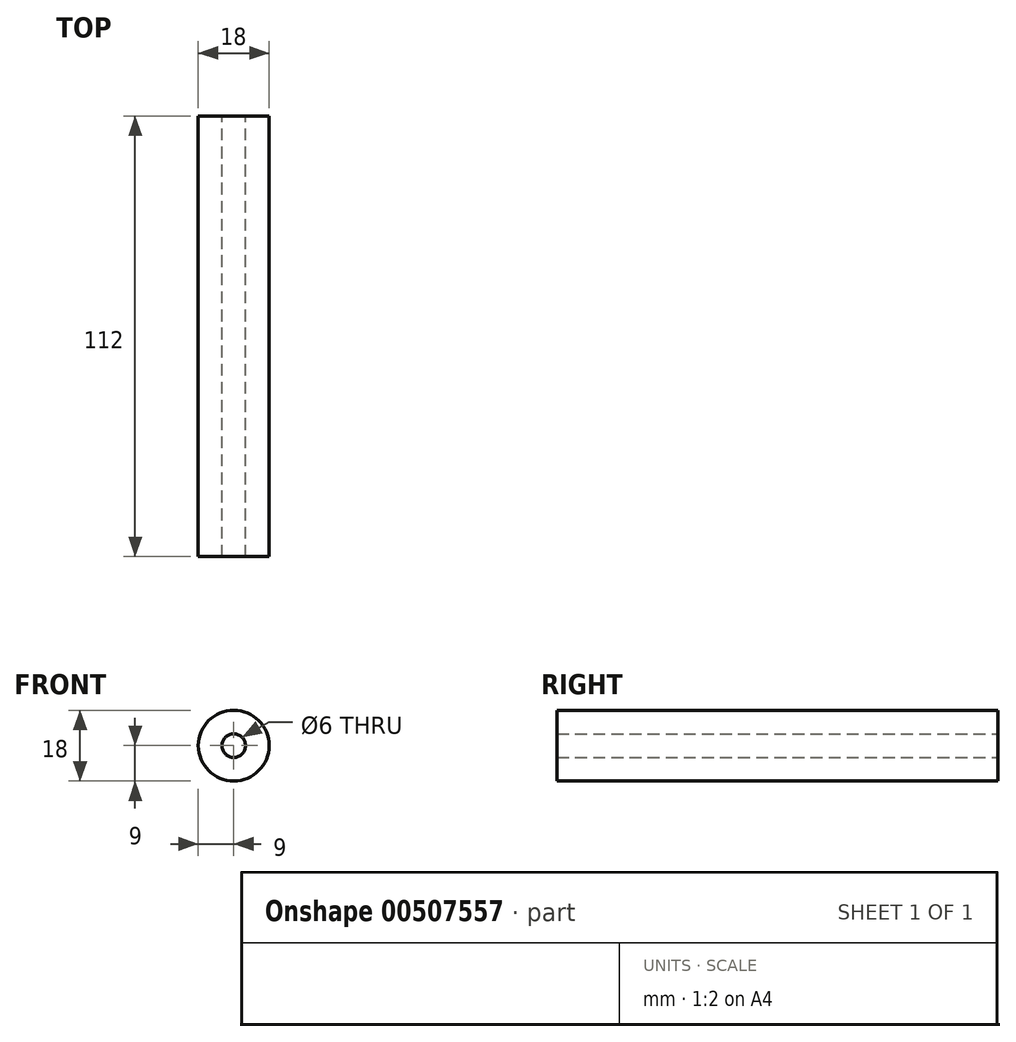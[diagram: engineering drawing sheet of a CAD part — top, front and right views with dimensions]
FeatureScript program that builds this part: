
annotation { "Feature Type Name" : "Feature", "Feature Type Description" : "" }
export const myFeature = defineFeature(function(context is Context, id is Id, definition is map)
    precondition{}
    {
        {
            var Q0;
            Q0=qCreatedBy(makeId("Front.planeOp"),FACE);
            var sketch = newSketch(context, id + "F0", { "sketchPlane" : qUnion([Q0])});
            skCircle(sketch, "E0", {"center": v(0, 0) * mm, "radius": 9 * mm});
            skCircle(sketch, "E1", {"center": v(0, 0) * mm, "radius": 3 * mm});
            skSolve(sketch);
        }
        {
            var Q0;
            Q0=makeQuery(id+"F0.imprint","IMPRINT",FACE,{"disambiguationData":[TD([[makeQuery(id+"F0.imprint","IMPRINT",EDGE,{"derivedFrom":sQuery(id+"F0.wireOp",EDGE,"E0")}),1.0]])]});
            extrude(context, id + "F1", {"entities" : qUnion([Q0]), "depth" : 112 * mm, "offsetDistance" : 25 * mm});
        }
    });
